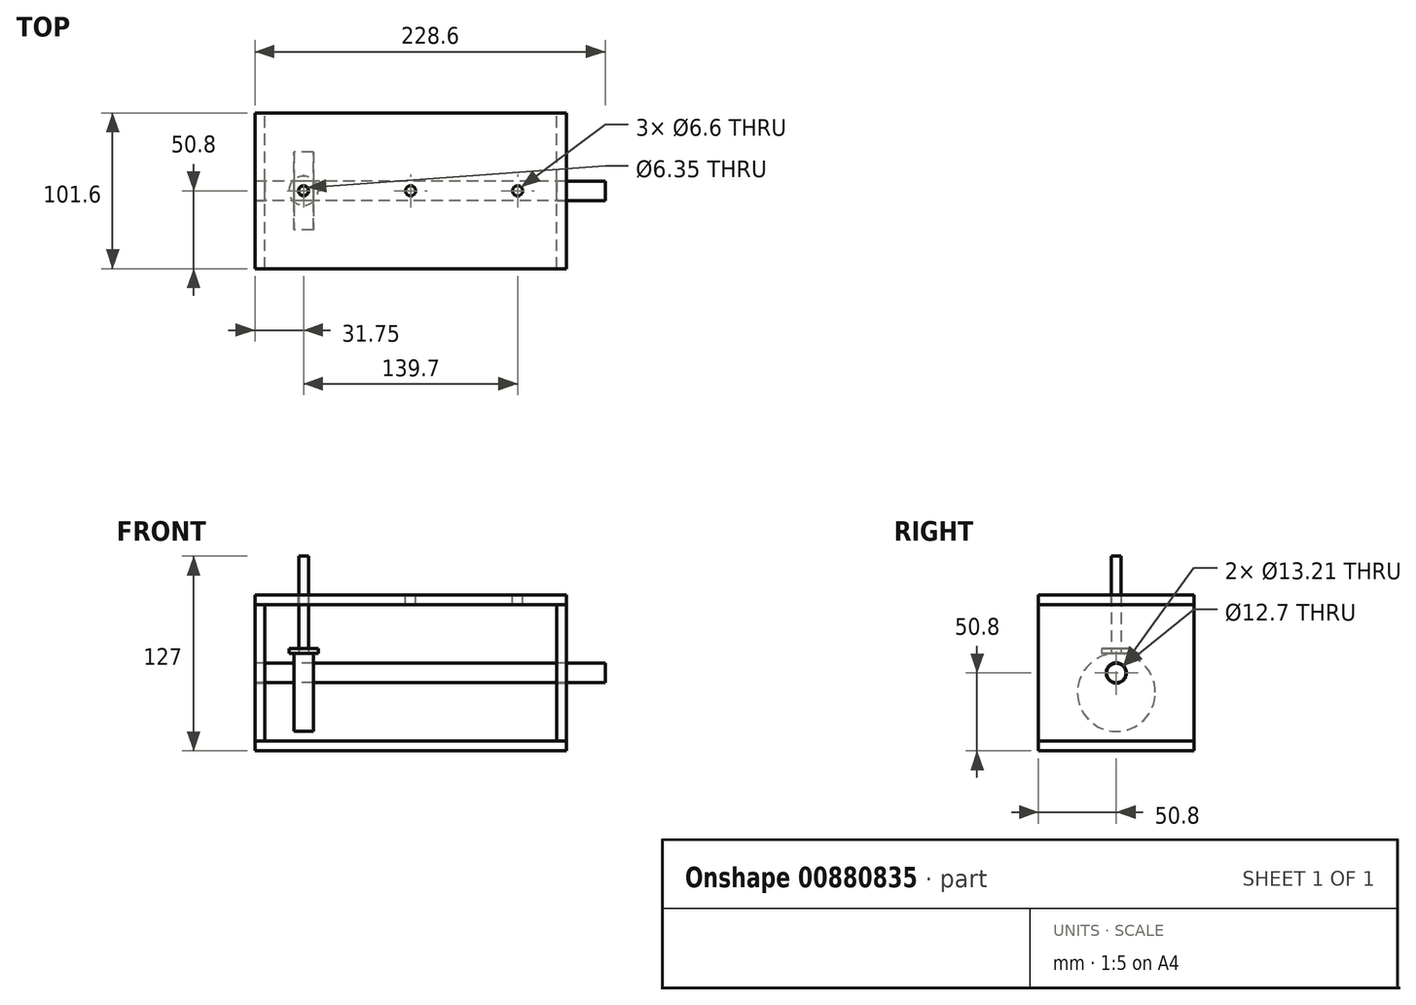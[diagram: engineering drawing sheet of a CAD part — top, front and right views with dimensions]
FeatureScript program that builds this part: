
annotation { "Feature Type Name" : "Feature", "Feature Type Description" : "" }
export const myFeature = defineFeature(function(context is Context, id is Id, definition is map)
    precondition{}
    {
        {
            var Q0;
            Q0=qCreatedBy(makeId("Front.planeOp"),FACE);
            var sketch = newSketch(context, id + "F0", { "sketchPlane" : qUnion([Q0])});
            skLineSegment(sketch, "E0.bottom", {"start": v(-101.6, 6.35) * mm, "end": v(101.6, 6.35) * mm});
            skLineSegment(sketch, "E0.top", {"start": v(-101.6, 0) * mm, "end": v(101.6, 0) * mm});
            skLineSegment(sketch, "E0.left", {"start": v(-101.6, 6.35) * mm, "end": v(-101.6, 0) * mm});
            skLineSegment(sketch, "E0.right", {"start": v(101.6, 6.35) * mm, "end": v(101.6, 0) * mm});
            skLineSegment(sketch, "E1", {"start": v(-101.6, 50.8) * mm, "end": v(-95.25, 50.8) * mm, "construction": true});
            skLineSegment(sketch, "E2", {"start": v(0, 6.35) * mm, "end": v(0, 0) * mm, "construction": true});
            skLineSegment(sketch, "E3.bottom", {"start": v(-101.6, 95.25) * mm, "end": v(101.6, 95.25) * mm});
            skLineSegment(sketch, "E3.top", {"start": v(-101.6, 101.6) * mm, "end": v(101.6, 101.6) * mm});
            skLineSegment(sketch, "E3.left", {"start": v(-101.6, 95.25) * mm, "end": v(-101.6, 101.6) * mm});
            skLineSegment(sketch, "E3.right", {"start": v(101.6, 95.25) * mm, "end": v(101.6, 101.6) * mm});
            skLineSegment(sketch, "E4", {"start": v(-101.6, 95.25) * mm, "end": v(-101.6, 6.35) * mm});
            skLineSegment(sketch, "E5", {"start": v(-95.25, 95.25) * mm, "end": v(-95.25, 6.35) * mm});
            skLineSegment(sketch, "E6", {"start": v(95.25, 95.25) * mm, "end": v(95.25, 6.35) * mm});
            skLineSegment(sketch, "E7", {"start": v(101.6, 95.25) * mm, "end": v(101.6, 6.35) * mm});
            skLineSegment(sketch, "E8", {"start": v(95.25, 50.8) * mm, "end": v(101.6, 50.8) * mm, "construction": true});
            skLineSegment(sketch, "E9.bottom", {"start": v(-76.2, 63.5) * mm, "end": v(-63.5, 63.5) * mm});
            skLineSegment(sketch, "E9.top", {"start": v(-76.2, 12.7) * mm, "end": v(-63.5, 12.7) * mm});
            skLineSegment(sketch, "E9.left", {"start": v(-76.2, 63.5) * mm, "end": v(-76.2, 12.7) * mm});
            skLineSegment(sketch, "E9.right", {"start": v(-63.5, 63.5) * mm, "end": v(-63.5, 12.7) * mm});
            skLineSegment(sketch, "E10.bottom", {"start": v(-6.35, 82.55) * mm, "end": v(6.35, 82.55) * mm});
            skLineSegment(sketch, "E10.top", {"start": v(-6.35, 31.75) * mm, "end": v(6.35, 31.75) * mm});
            skLineSegment(sketch, "E10.left", {"start": v(-6.35, 82.55) * mm, "end": v(-6.35, 31.75) * mm});
            skLineSegment(sketch, "E10.right", {"start": v(6.35, 82.55) * mm, "end": v(6.35, 31.75) * mm});
            skLineSegment(sketch, "E11.bottom", {"start": v(63.5, 82.55) * mm, "end": v(76.2, 82.55) * mm});
            skLineSegment(sketch, "E11.top", {"start": v(63.5, 31.75) * mm, "end": v(76.2, 31.75) * mm});
            skLineSegment(sketch, "E11.left", {"start": v(63.5, 82.55) * mm, "end": v(63.5, 31.75) * mm});
            skLineSegment(sketch, "E11.right", {"start": v(76.2, 82.55) * mm, "end": v(76.2, 31.75) * mm});
            skLineSegment(sketch, "E12", {"start": v(-76.2, 38.1) * mm, "end": v(-63.5, 38.1) * mm});
            skLineSegment(sketch, "E13", {"start": v(-6.35, 57.15) * mm, "end": v(6.35, 57.15) * mm});
            skLineSegment(sketch, "E14", {"start": v(63.5, 57.15) * mm, "end": v(76.2, 57.15) * mm});
            skLineSegment(sketch, "E15", {"start": v(-95.25, 50.8) * mm, "end": v(95.25, 50.8) * mm});
            skLineSegment(sketch, "E16", {"start": v(-69.85, 50.8) * mm, "end": v(-69.85, 38.1) * mm, "construction": true});
            skLineSegment(sketch, "E17", {"start": v(69.85, 57.15) * mm, "end": v(69.85, 50.8) * mm, "construction": true});
            skLineSegment(sketch, "E18", {"start": v(0, 57.15) * mm, "end": v(0, 50.8) * mm, "construction": true});
            skLineSegment(sketch, "E19", {"start": v(-69.85, 63.5) * mm, "end": v(-69.85, 127) * mm, "construction": true});
            skLineSegment(sketch, "E20", {"start": v(0, 82.55) * mm, "end": v(0, 146.05) * mm, "construction": true});
            skPoint(sketch, "E20.endSnap0", {"position": v(0, 101.6) * mm});
            skLineSegment(sketch, "E21", {"start": v(69.85, 82.55) * mm, "end": v(69.85, 146.05) * mm, "construction": true});
            skSolve(sketch);
        }
        {
            var Q0;
            Q0=makeQuery(id+"F0.imprint","IMPRINT",FACE,{"disambiguationData":[TD([[makeQuery(id+"F0.imprint","IMPRINT",EDGE,{"derivedFrom":sQuery(id+"F0.wireOp",EDGE,"E0.bottom")}),-1.0]])]});
            var Q1;
            Q1=makeQuery(id+"F0.imprint","IMPRINT",FACE,{"disambiguationData":[TD([[makeQuery(id+"F0.imprint","IMPRINT",EDGE,{"derivedFrom":sQuery(id+"F0.wireOp",EDGE,"E3.top")}),-1.0]])]});
            extrude(context, id + "F1", {"entities" : qUnion([Q0, Q1]), "endBound" : BoundingType.SYMMETRIC, "depth" : 101.6 * mm, "offsetDistance" : 25.4 * mm});
        }
        {
            var Q0;
            {var subQ4=sQuery(id+"F0.wireOp",EDGE,"E4");Q0=makeQuery(id+"F0.imprint","IMPRINT",FACE,{"disambiguationData":[TD([[makeQuery(id+"F0.imprint","IMPRINT",EDGE,{"derivedFrom":subQ4}),1.0]])]});}
            var Q1;
            {var subQ6=sQuery(id+"F0.wireOp",EDGE,"E7");Q1=makeQuery(id+"F0.imprint","IMPRINT",FACE,{"disambiguationData":[TD([[makeQuery(id+"F0.imprint","IMPRINT",EDGE,{"derivedFrom":subQ6}),-1.0]])]});}
            var Q2;
            Q2=makeQuery(id+"F1.opExtrude","CAP_FACE",FACE,{"disambiguationData":[OSD([sQuery(id+"F0.wireOp",EDGE,"E0.bottom"),sQuery(id+"F0.wireOp",EDGE,"E0.top"),sQuery(id+"F0.wireOp",EDGE,"E0.left"),sQuery(id+"F0.wireOp",EDGE,"E0.right")])],"isStart":false});
            var Q3;
            Q3=makeQuery(id+"F1.opExtrude","CAP_FACE",FACE,{"disambiguationData":[OSD([sQuery(id+"F0.wireOp",EDGE,"E3.bottom"),sQuery(id+"F0.wireOp",EDGE,"E3.top"),sQuery(id+"F0.wireOp",EDGE,"E3.left"),sQuery(id+"F0.wireOp",EDGE,"E3.right")])],"isStart":true});
            extrude(context, id + "F2", {"entities" : qUnion([Q0, Q1]), "endBound" : BoundingType.UP_TO_SURFACE, "depth" : 101.6 * mm, "endBoundEntityFace" : qUnion([Q2]), "offsetDistance" : 25.4 * mm, "hasSecondDirection" : true, "secondDirectionBound" : SecondDirectionBoundingType.UP_TO_SURFACE, "secondDirectionOppositeDirection" : true, "secondDirectionDepth" : 25.4 * mm, "secondDirectionBoundEntityFace" : qUnion([Q3])});
        }
        {
            var Q0;
            Q0=makeQuery(id+"F2.opExtrude","SWEPT_FACE",FACE,{"disambiguationData":[OSD([sQuery(id+"F0.wireOp",EDGE,"E7")])]});
            var sketch = newSketch(context, id + "F3", { "sketchPlane" : qUnion([Q0])});
            skCircle(sketch, "E22", {"center": v(0, 50.8) * mm, "radius": 6.35 * mm});
            skCircle(sketch, "E23", {"center": v(0, 50.8) * mm, "radius": 6.6 * mm});
            skSolve(sketch);
        }
        {
            var Q0;
            Q0=makeQuery(id+"F3.imprint","IMPRINT",FACE,{"disambiguationData":[TD([[makeQuery(id+"F3.imprint","IMPRINT",EDGE,{"derivedFrom":sQuery(id+"F3.wireOp",EDGE,"E22")}),-1.0]])]});
            var Q1;
            Q1=makeQuery(id+"F3.imprint","IMPRINT",FACE,{"disambiguationData":[TD([[makeQuery(id+"F3.imprint","IMPRINT",EDGE,{"derivedFrom":sQuery(id+"F3.wireOp",EDGE,"E22")}),1.0]])]});
            extrude(context, id + "F4", {"entities" : qUnion([Q0, Q1]), "operationType" : NewBodyOperationType.REMOVE, "endBound" : BoundingType.THROUGH_ALL, "oppositeDirection" : true, "depth" : 25.4 * mm, "offsetDistance" : 25.4 * mm});
        }
        {
            var Q0;
            Q0=makeQuery(id+"F3.imprint","IMPRINT",FACE,{"disambiguationData":[TD([[makeQuery(id+"F3.imprint","IMPRINT",EDGE,{"derivedFrom":sQuery(id+"F3.wireOp",EDGE,"E22")}),1.0]])]});
            var Q1;
            Q1=makeQuery(id+"F2.opExtrude","SWEPT_FACE",FACE,{"disambiguationData":[OSD([sQuery(id+"F0.wireOp",EDGE,"E4")])]});
            extrude(context, id + "F5", {"entities" : qUnion([Q0]), "depth" : 25.4 * mm, "offsetDistance" : 25.4 * mm, "hasSecondDirection" : true, "secondDirectionBound" : SecondDirectionBoundingType.UP_TO_SURFACE, "secondDirectionOppositeDirection" : true, "secondDirectionDepth" : 25.4 * mm, "secondDirectionBoundEntityFace" : qUnion([Q1])});
        }
        {
            var Q0;
            {var subQ0=sQuery(id+"F0.wireOp",EDGE,"E9.top");Q0=makeQuery(id+"F0.imprint","IMPRINT",FACE,{"disambiguationData":[TD([[makeQuery(id+"F0.imprint","IMPRINT",EDGE,{"derivedFrom":subQ0}),1.0]])]});}
            var Q1;
            Q1=sQuery(id+"F0.wireOp",EDGE,"E12");
            revolve(context, id + "F6", {"surfaceOperationType" : NewSurfaceOperationType.NEW, "entities" : qUnion([Q0]), "axis" : qUnion([Q1]), "revolveType" : RevolveType.FULL});
        }
        {
            var Q0;
            Q0=makeQuery(id+"F5.opExtrude","SWEPT_BODY",BODY,{"disambiguationData":[OSD([sQuery(id+"F3.wireOp",EDGE,"E22")])]});
            var Q1;
            Q1=makeQuery(id+"F6.opRevolve","SWEPT_BODY",BODY,{"disambiguationData":[OSD([sQuery(id+"F0.wireOp",EDGE,"E9.top"),sQuery(id+"F0.wireOp",EDGE,"E9.left"),sQuery(id+"F0.wireOp",EDGE,"E9.right"),sQuery(id+"F0.wireOp",EDGE,"E12")])]});
            booleanBodies(context, id + "F7", {"operationType" : BooleanOperationType.SUBTRACTION, "tools" : qUnion([Q0]), "targets" : qUnion([Q1]), "keepTools" : true});
        }
        {
            var Q0;
            Q0=makeQuery(id+"F1.opExtrude","SWEPT_FACE",FACE,{"disambiguationData":[OSD([sQuery(id+"F0.wireOp",EDGE,"E3.top")])]});
            var sketch = newSketch(context, id + "F8", { "sketchPlane" : qUnion([Q0])});
            skPoint(sketch, "E24", {"position": v(-69.85, 0) * mm});
            skPoint(sketch, "E25", {"position": v(69.85, 0) * mm});
            skPoint(sketch, "E26", {"position": v(0, 0) * mm});
            skSolve(sketch);
        }
        {
            var Q0;
            Q0=sQuery(id+"F8.wireOp",VERTEX,"E24");
            var Q1;
            Q1=sQuery(id+"F8.wireOp",VERTEX,"E25");
            var Q2;
            Q2=sQuery(id+"F8.wireOp",VERTEX,"E26");
            var Q3;
            Q3=makeQuery(id+"F1.opExtrude","SWEPT_BODY",BODY,{"disambiguationData":[OSD([sQuery(id+"F0.wireOp",EDGE,"E3.bottom"),sQuery(id+"F0.wireOp",EDGE,"E3.top"),sQuery(id+"F0.wireOp",EDGE,"E3.left"),sQuery(id+"F0.wireOp",EDGE,"E3.right")])]});
            hole(context, id + "F9", {"style" : HoleStyle.SIMPLE, "endStyle" : HoleEndStyle.THROUGH, "holeDiameter" : 6.6 * mm, "majorDiameter" : 6.35 * mm, "isTappedThrough" : true, "tappedDepth" : 12.7 * mm, "tapClearance" : 3, "locations" : qUnion([Q0, Q1, Q2]), "scope" : qUnion([Q3])});
        }
        {
            var Q0;
            Q0=qCreatedBy(makeId("Top.planeOp"),FACE);
            var Q1;
            Q1=sQuery(id+"F0.wireOp",VERTEX,"E19.start");
            cPlane(context, id + "F10", {"entities" : qUnion([Q0, Q1]), "cplaneType" : CPlaneType.PLANE_POINT, "offset" : 25.4 * mm, "width" : 152.4 * mm, "height" : 152.4 * mm});
        }
        {
            var Q0;
            Q0=qCreatedBy(id+"F10.planeOp",FACE);
            var sketch = newSketch(context, id + "F11", { "sketchPlane" : qUnion([Q0])});
            skCircle(sketch, "E27", {"center": v(-69.85, 0) * mm, "radius": 9.53 * mm});
            skCircle(sketch, "E28", {"center": v(-69.85, 0) * mm, "radius": 3.18 * mm});
            skSolve(sketch);
        }
        {
            var Q0;
            Q0=makeQuery(id+"F11.imprint","IMPRINT",FACE,{"disambiguationData":[TD([[makeQuery(id+"F11.imprint","IMPRINT",EDGE,{"derivedFrom":sQuery(id+"F11.wireOp",EDGE,"E28")}),1.0]])]});
            var Q1;
            Q1=sQuery(id+"F0.wireOp",VERTEX,"E19.end");
            extrude(context, id + "F12", {"entities" : qUnion([Q0]), "endBound" : BoundingType.UP_TO_VERTEX, "depth" : 25.4 * mm, "endBoundEntityVertex" : qUnion([Q1]), "offsetDistance" : 25.4 * mm});
        }
        {
            var Q0;
            Q0=makeQuery(id+"F11.imprint","IMPRINT",FACE,{"disambiguationData":[TD([[makeQuery(id+"F11.imprint","IMPRINT",EDGE,{"derivedFrom":sQuery(id+"F11.wireOp",EDGE,"E27")}),1.0]])]});
            extrude(context, id + "F13", {"entities" : qUnion([Q0]), "depth" : 3.17 * mm, "offsetDistance" : 25.4 * mm});
        }
    });
